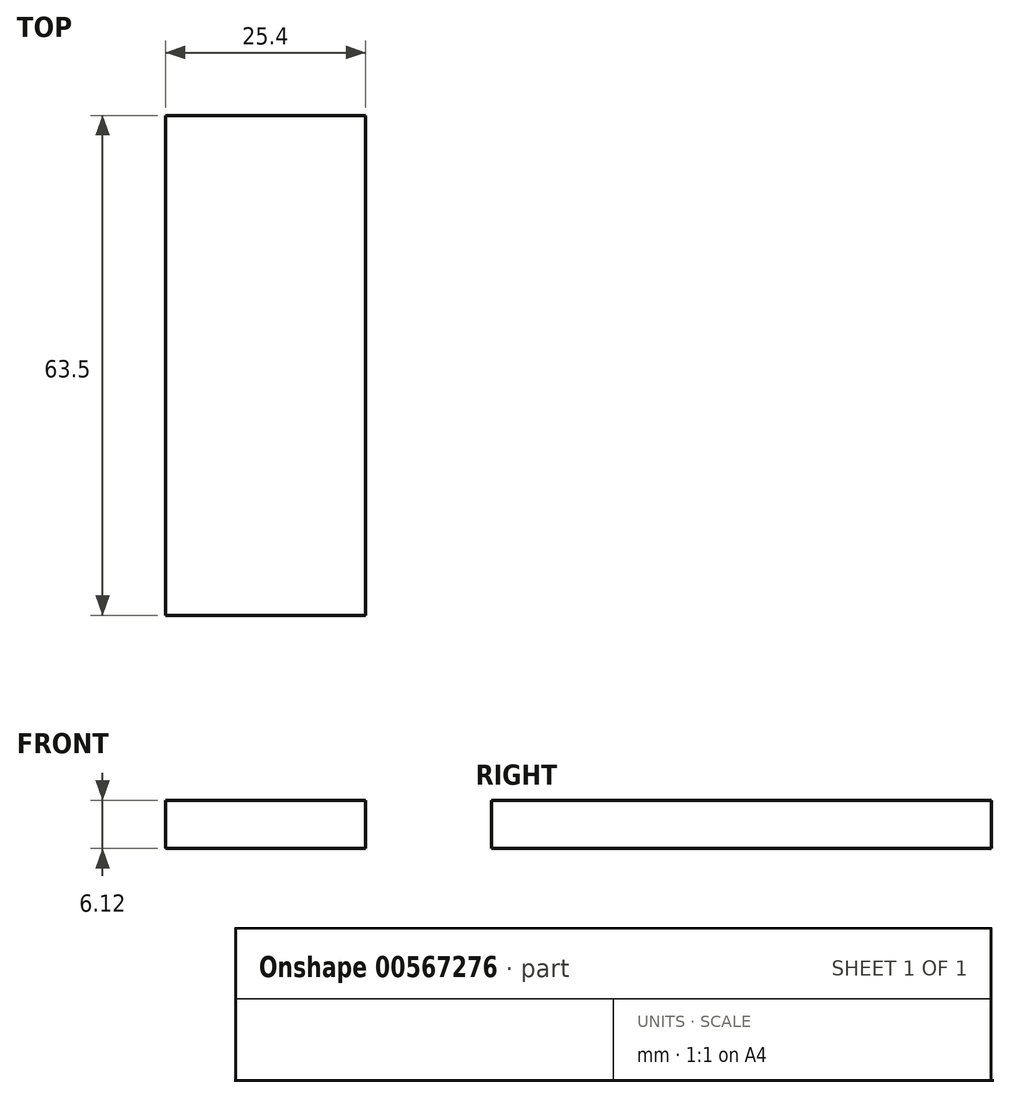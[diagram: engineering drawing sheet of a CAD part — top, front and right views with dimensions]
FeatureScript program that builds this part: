
annotation { "Feature Type Name" : "Feature", "Feature Type Description" : "" }
export const myFeature = defineFeature(function(context is Context, id is Id, definition is map)
    precondition{}
    {
        {
            var Q0;
            Q0=qCreatedBy(makeId("Top.planeOp"),FACE);
            var sketch = newSketch(context, id + "F0", { "sketchPlane" : qUnion([Q0])});
            skLineSegment(sketch, "E0.bottom", {"start": v(12.7, -31.75) * mm, "end": v(-12.7, -31.75) * mm});
            skLineSegment(sketch, "E0.top", {"start": v(12.7, 31.75) * mm, "end": v(-12.7, 31.75) * mm});
            skLineSegment(sketch, "E0.left", {"start": v(12.7, -31.75) * mm, "end": v(12.7, 31.75) * mm});
            skLineSegment(sketch, "E0.right", {"start": v(-12.7, -31.75) * mm, "end": v(-12.7, 31.75) * mm});
            skPoint(sketch, "E0.middle", {"position": v(0, 0) * mm});
            skSolve(sketch);
        }
        {
            var Q0;
            Q0 = qSketchRegion(id + "F0", true);
            extrude(context, id + "F1", {"entities" : qUnion([Q0]), "depth" : 24.5 / 4 * mm, "offsetDistance" : 25 * mm});
        }
    });
